# Revit family: IS_Tempo_T3311_BIM_DE
name_source: partatom
category: Plumbing Fixtures
revit_build: Autodesk Revit MEP 2016 (Build: 20161004_0715(x64)
units: mm (PartAtom-declared; Revit-internal decimal feet)

## family parameters
Cut with Voids When Loaded = No
Host = Face
OmniClass Number = 23.45.05.21.11.11
OmniClass Title = Water Operated Water Closets
Part Type = Normal
Room Calculation Point = No
Round Connector Dimension = Use Diameter
Shared = Yes

## types (1)
- T331101 - TEMPO W/H PAN HO WHITE BOXED
    Accessories = www.idealstandard.de\ersatzteile
    AreaUnits = millimeters
    Assembly Code = C1030200
    AssetType = Fixed
    BIMObjectName = ISI_IdealStandard_WCPans_TEMPO_T331101
    BarCode = 8014140410461
    Brand = Ideal Standard
    CWFU = 0
    CodePerformance = DIN EN 997 CL1-6AC/5A, DIN EN 33
    Color = White
    ConnectionType = Plumbing
    Cost = 0 $
    CurrencyUnit = €
    Default Elevation = 400 mm  [stored 1.31234 ft]
    Description = Tempo Wall hung Pan
    DurationUnit = year
    ExpectedLife = 25
    Features = EUROVIT PLUS wall mounted bowl 360x530mm, wash-down
    Finish = White
    GrossWeight = 19,8 kg
    HWFU = 0
    IfcExportAs = IfcSanitaryTerminalType
    IfcExportType = TOILETPAN
    InstallationDate = 1900-12-31T23:59:59
    InstallationInstructions = www.idealstandard.de\produkte
    LinearUnits = millimeters
    ManufacturerURL = www.idealstandard.de
    Material = Vitreous china
    Model = T331101
    ModelNumber = T331101
    ModelReference = IS Wand-T-WC EUROVIT+, 360x530x350mm, Weiß
    NBSDescription = WC pans
    NBSReference = 45-35-70/384
    Name = ISI_IdealStandard_WCPans_TEMPO_T331101
    NettWeight = 17,58 kg
    NominalDepth = 0 mm  [stored 0 ft]
    NominalHeight = 348 mm
    NominalLength = 530 mm
    NominalWidth = 360 mm
    PanColor = White
    PanMaterial = Vitreous china
    PanMounting = BackToWall
    ProductInformation = www.idealstandard.de
    Shape = Sculptured
    Size = 530 x 360 x 350 mm
    Space = Internal
    SpilloverLevel = 0 mm  [stored 0 ft]
    ToiletPanType = WashDown
    ToiletType = Other
    URL = www.idealstandard.de
    Uniclass2015Code = Pr_40_20_93_94
    Uniclass2015Title = WC pans
    Uniclass2015Version = Products v1.1
    Version = 1
    VolumeUnits = Litres
    WFU = 0

note: [stored X ft] marks values corroborated as IEEE doubles in the binary element streams (Revit-internal decimal feet)

## geometry (parser evidence)
native form markers: Blend x4, Sweep x1
no freeform markers — native parametric forms only
